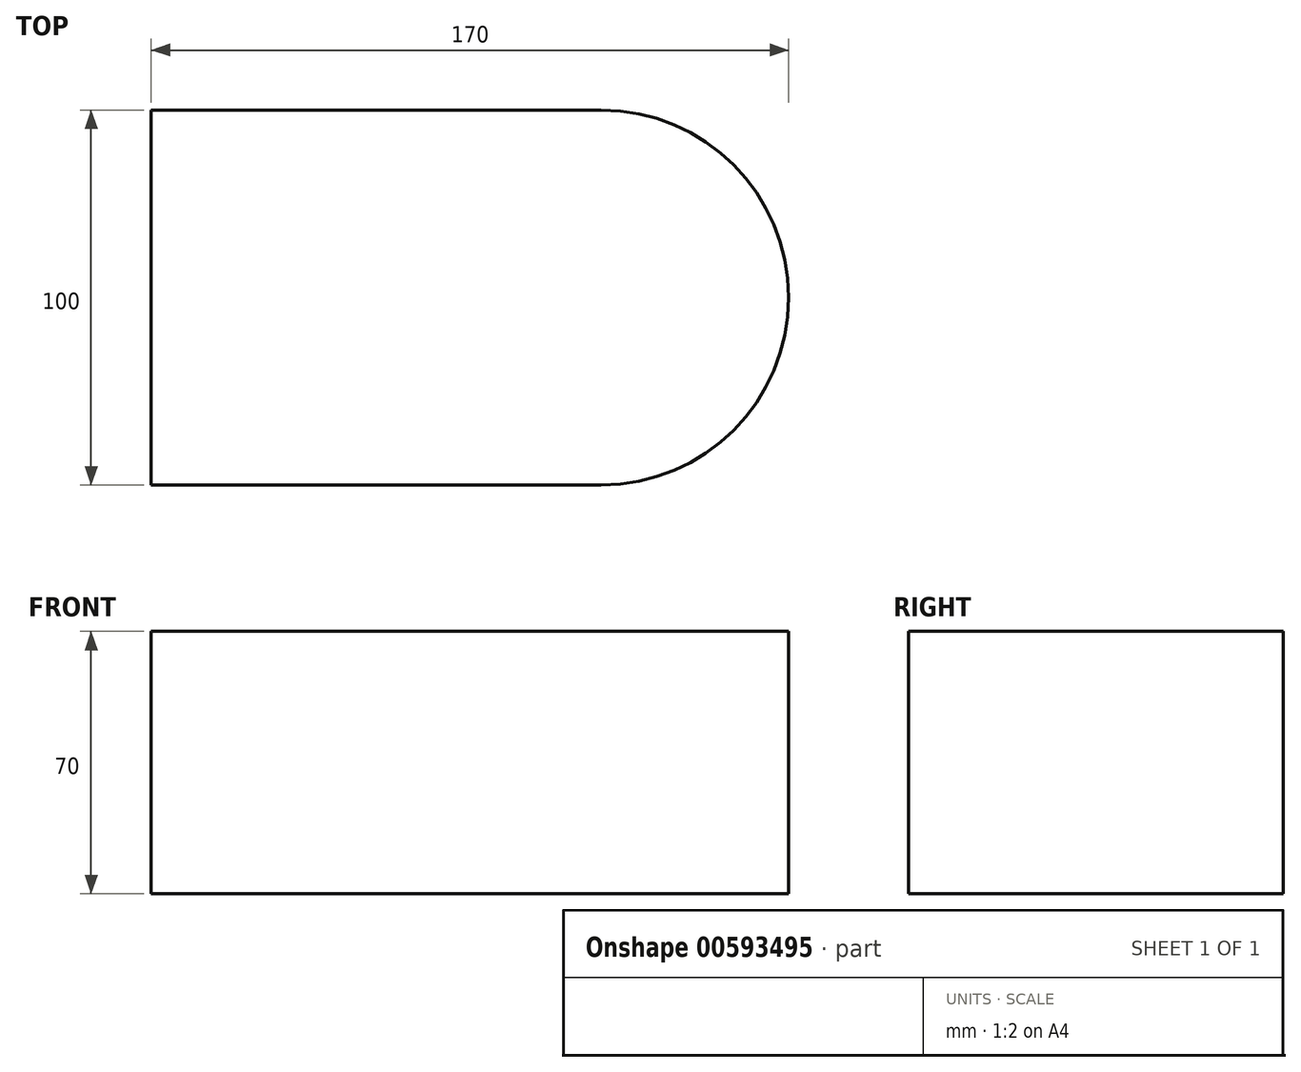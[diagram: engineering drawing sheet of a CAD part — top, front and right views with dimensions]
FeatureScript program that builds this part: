
annotation { "Feature Type Name" : "Feature", "Feature Type Description" : "" }
export const myFeature = defineFeature(function(context is Context, id is Id, definition is map)
    precondition{}
    {
        {
            var Q0;
            Q0=qCreatedBy(makeId("Top.planeOp"),FACE);
            var sketch = newSketch(context, id + "F0", { "sketchPlane" : qUnion([Q0])});
            skLineSegment(sketch, "E0.bottom", {"start": v(-120, -50) * mm, "end": v(0, -50) * mm});
            skLineSegment(sketch, "E0.top", {"start": v(-120, 50) * mm, "end": v(0, 50) * mm});
            skLineSegment(sketch, "E0.left", {"start": v(-120, -50) * mm, "end": v(-120, 50) * mm});
            skLineSegment(sketch, "E0.right", {"start": v(0, -50) * mm, "end": v(0, 50) * mm});
            skArc(sketch, "E1", {"start": v(0, -50) * mm, "mid": v(50, 0) * mm, "end": v(0, 50) * mm});
            skLineSegment(sketch, "E2", {"start": v(50, 0) * mm, "end": v(-120, 0) * mm, "construction": true});
            skPoint(sketch, "E3", {"position": v(-35, 0) * mm});
            skLineSegment(sketch, "E4", {"start": v(0, 0) * mm, "end": v(0, -28.69) * mm, "construction": true});
            skSolve(sketch);
        }
        {
            var Q0;
            Q0 = qSketchRegion(id + "F0", true);
            extrude(context, id + "F1", {"entities" : qUnion([Q0]), "depth" : 70 * mm, "offsetDistance" : 25 * mm});
        }
    });
